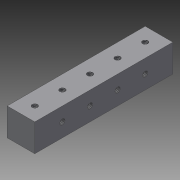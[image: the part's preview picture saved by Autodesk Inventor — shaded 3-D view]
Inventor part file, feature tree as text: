
AUTODESK INVENTOR PART (.ipt)
format: ipt  version: 2015 (Build 190159000, 159)  size: 101,376 bytes
history: native  units: in
note: dims shown in document units (in); Inventor stores cm internally (conversion verified against a paired STEP export)
features: sketch x3, hole x2, extrude x1
ambient origin geometry x8: Origin, YZ Plane, XZ Plane, XY Plane, X Axis, Y Axis, Z Axis, Center Point
bodies: Solid1 (feature_tree)
feature tree (6):
  extrude  "Extrusion1"  Depth=0.5in
  hole  "Hole1"  [1 undecoded]
  hole  "Hole2"  [1 undecoded]
  sketch  "Sketch1"  dims[d0=2.5in d1=0.5in]
  sketch  "Sketch2"  dims[d2=0.5in d3=0.0in d4=0.5in]
  sketch  "Sketch3"  dims[d5=0.5in d6=0.5in d8=0.097in d9=1.0in d10=0.375in d11=0.25in d12=0.5635in d13=0.346in d14=0.8108in d15=0.25in d16=0.5in d17=0.5in d18=0.5in d19=0.5in d20=0.097in d21=0.5in d22=0.375in d23=0.25in d24=0.5635in d25=0.346in d26=0.8108in]
note: 2 required parameter values undecoded (feature->parameter linkage not recoverable at this tier; creation-order binding heuristic only, values carry confidence <= 0.55)
